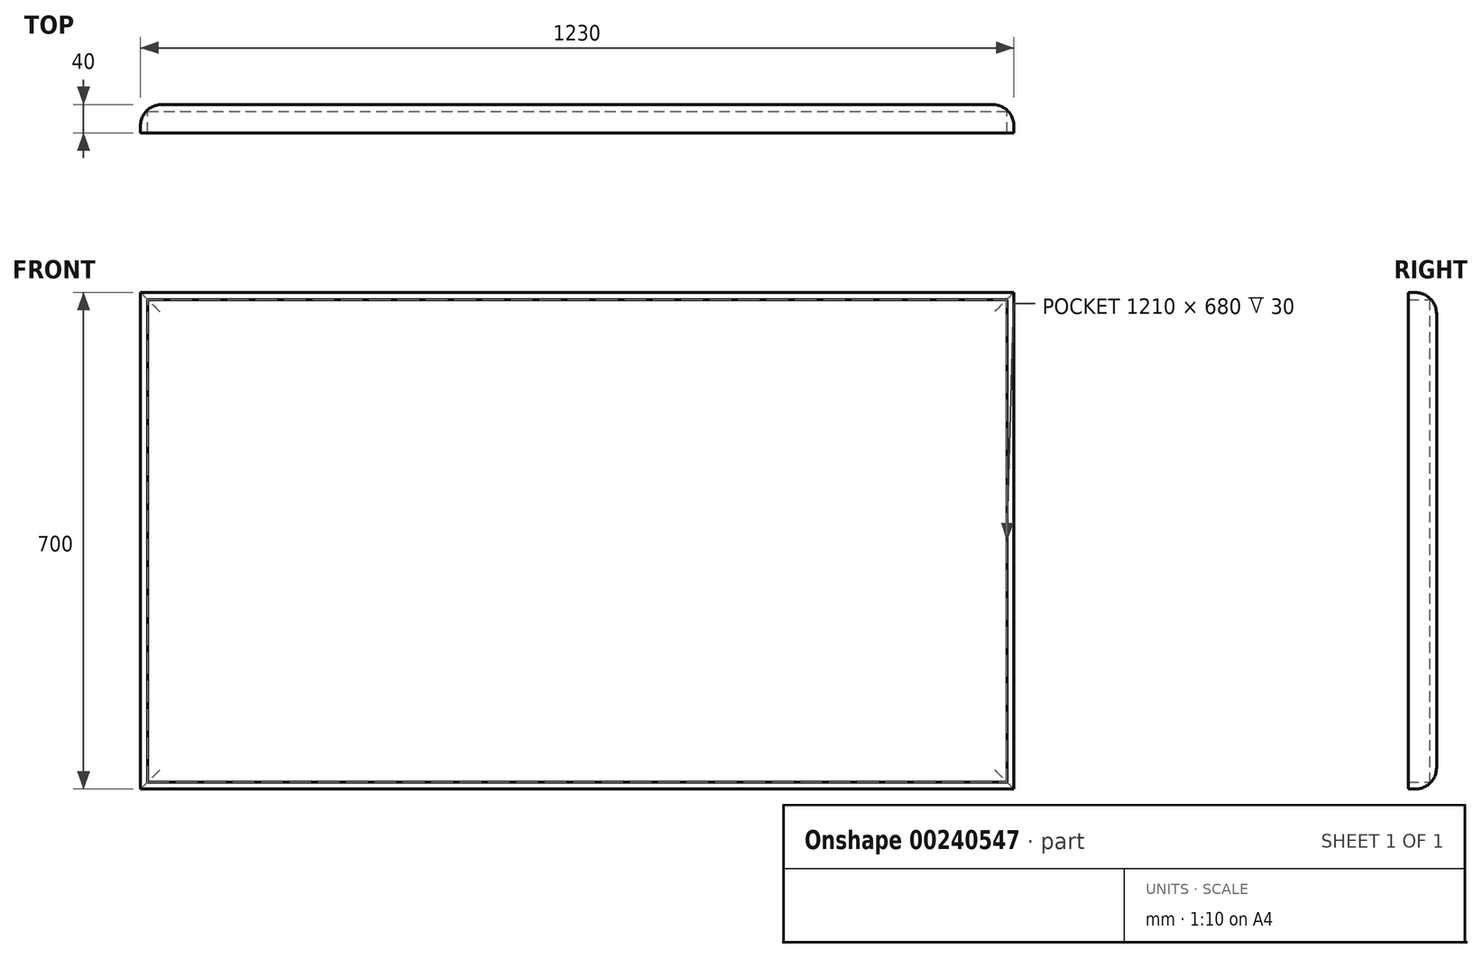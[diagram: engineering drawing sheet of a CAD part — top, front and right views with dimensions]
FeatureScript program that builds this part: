
annotation { "Feature Type Name" : "Feature", "Feature Type Description" : "" }
export const myFeature = defineFeature(function(context is Context, id is Id, definition is map)
    precondition{}
    {
        {
            var Q0;
            Q0=qCreatedBy(makeId("Front.planeOp"),FACE);
            var sketch = newSketch(context, id + "F0", { "sketchPlane" : qUnion([Q0])});
            skLineSegment(sketch, "E0.bottom", {"start": v(-607.09, 364.95) * mm, "end": v(622.91, 364.95) * mm});
            skLineSegment(sketch, "E0.top", {"start": v(-607.09, -335.05) * mm, "end": v(622.91, -335.05) * mm});
            skLineSegment(sketch, "E0.left", {"start": v(-607.09, 364.95) * mm, "end": v(-607.09, -335.05) * mm});
            skLineSegment(sketch, "E0.right", {"start": v(622.91, 364.95) * mm, "end": v(622.91, -335.05) * mm});
            skSolve(sketch);
        }
        {
            var Q0;
            Q0 = qSketchRegion(id + "F0", true);
            extrude(context, id + "F1", {"entities" : qUnion([Q0]), "depth" : 40 * mm});
        }
        {
            var Q0;
            Q0=makeQuery(id+"F1.opExtrude","CAP_FACE",FACE,{"disambiguationData":[OSD([sQuery(id+"F0.wireOp",EDGE,"E0.bottom"),sQuery(id+"F0.wireOp",EDGE,"E0.top"),sQuery(id+"F0.wireOp",EDGE,"E0.left"),sQuery(id+"F0.wireOp",EDGE,"E0.right")])],"isStart":false});
            var sketch = newSketch(context, id + "F2", { "sketchPlane" : qUnion([Q0])});
            skLineSegment(sketch, "E1.bottom", {"start": v(-587.09, 344.95) * mm, "end": v(602.91, 344.95) * mm});
            skLineSegment(sketch, "E1.top", {"start": v(-587.09, -315.05) * mm, "end": v(602.91, -315.05) * mm});
            skLineSegment(sketch, "E1.left", {"start": v(-587.09, 344.95) * mm, "end": v(-587.09, -315.05) * mm});
            skLineSegment(sketch, "E1.right", {"start": v(602.91, 344.95) * mm, "end": v(602.91, -315.05) * mm});
            skSolve(sketch);
        }
        {
            var Q0;
            Q0=makeQuery(id+"F1.opExtrude","CAP_FACE",FACE,{"disambiguationData":[OSD([sQuery(id+"F0.wireOp",EDGE,"E0.bottom"),sQuery(id+"F0.wireOp",EDGE,"E0.top"),sQuery(id+"F0.wireOp",EDGE,"E0.left"),sQuery(id+"F0.wireOp",EDGE,"E0.right")])],"isStart":false});
            shell(context, id + "F3", {"entities" : qUnion([Q0]), "thickness" : 10 * mm});
        }
        {
            var Q0;
            Q0=makeQuery(id+"F1.opExtrude","CAP_EDGE",EDGE,{"disambiguationData":[OSD([sQuery(id+"F0.wireOp",EDGE,"E0.top")])],"isStart":true});
            var Q1;
            Q1=makeQuery(id+"F1.opExtrude","CAP_EDGE",EDGE,{"disambiguationData":[OSD([sQuery(id+"F0.wireOp",EDGE,"E0.bottom")])],"isStart":true});
            var Q2;
            Q2=makeQuery(id+"F1.opExtrude","CAP_EDGE",EDGE,{"disambiguationData":[OSD([sQuery(id+"F0.wireOp",EDGE,"E0.left")])],"isStart":true});
            var Q3;
            Q3=makeQuery(id+"F1.opExtrude","CAP_EDGE",EDGE,{"disambiguationData":[OSD([sQuery(id+"F0.wireOp",EDGE,"E0.right")])],"isStart":true});
            fillet(context, id + "F4", {"entities" : qUnion([Q0, Q1, Q2, Q3]), "radius" : 30 * mm, "tangentPropagation" : true, "allowEdgeOverflow" : false});
        }
    });
